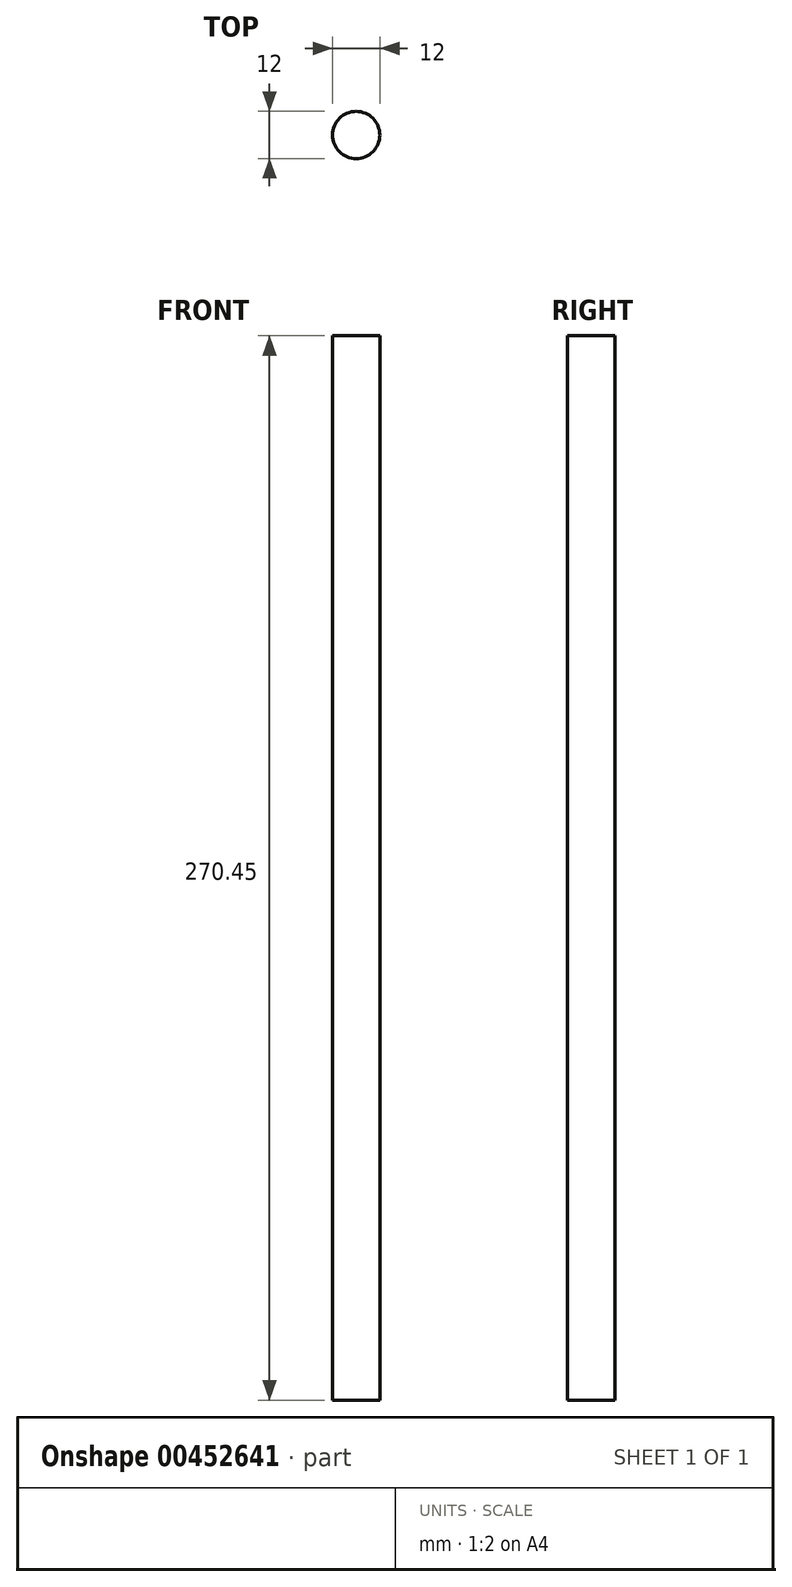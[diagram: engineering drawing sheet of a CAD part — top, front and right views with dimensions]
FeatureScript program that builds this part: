
annotation { "Feature Type Name" : "Feature", "Feature Type Description" : "" }
export const myFeature = defineFeature(function(context is Context, id is Id, definition is map)
    precondition{}
    {
        {
            var Q0;
            Q0=qCreatedBy(makeId("Top.planeOp"),FACE);
            var sketch = newSketch(context, id + "F0", { "sketchPlane" : qUnion([Q0])});
            skCircle(sketch, "E0", {"center": v(0, 0) * mm, "radius": 6 * mm});
            skSolve(sketch);
        }
        {
            var Q0;
            Q0=qSketchRegion(id+"F0",true);
            extrude(context, id + "F1", {"entities" : qUnion([Q0]), "depth" : 270.45 * mm});
        }
    });
